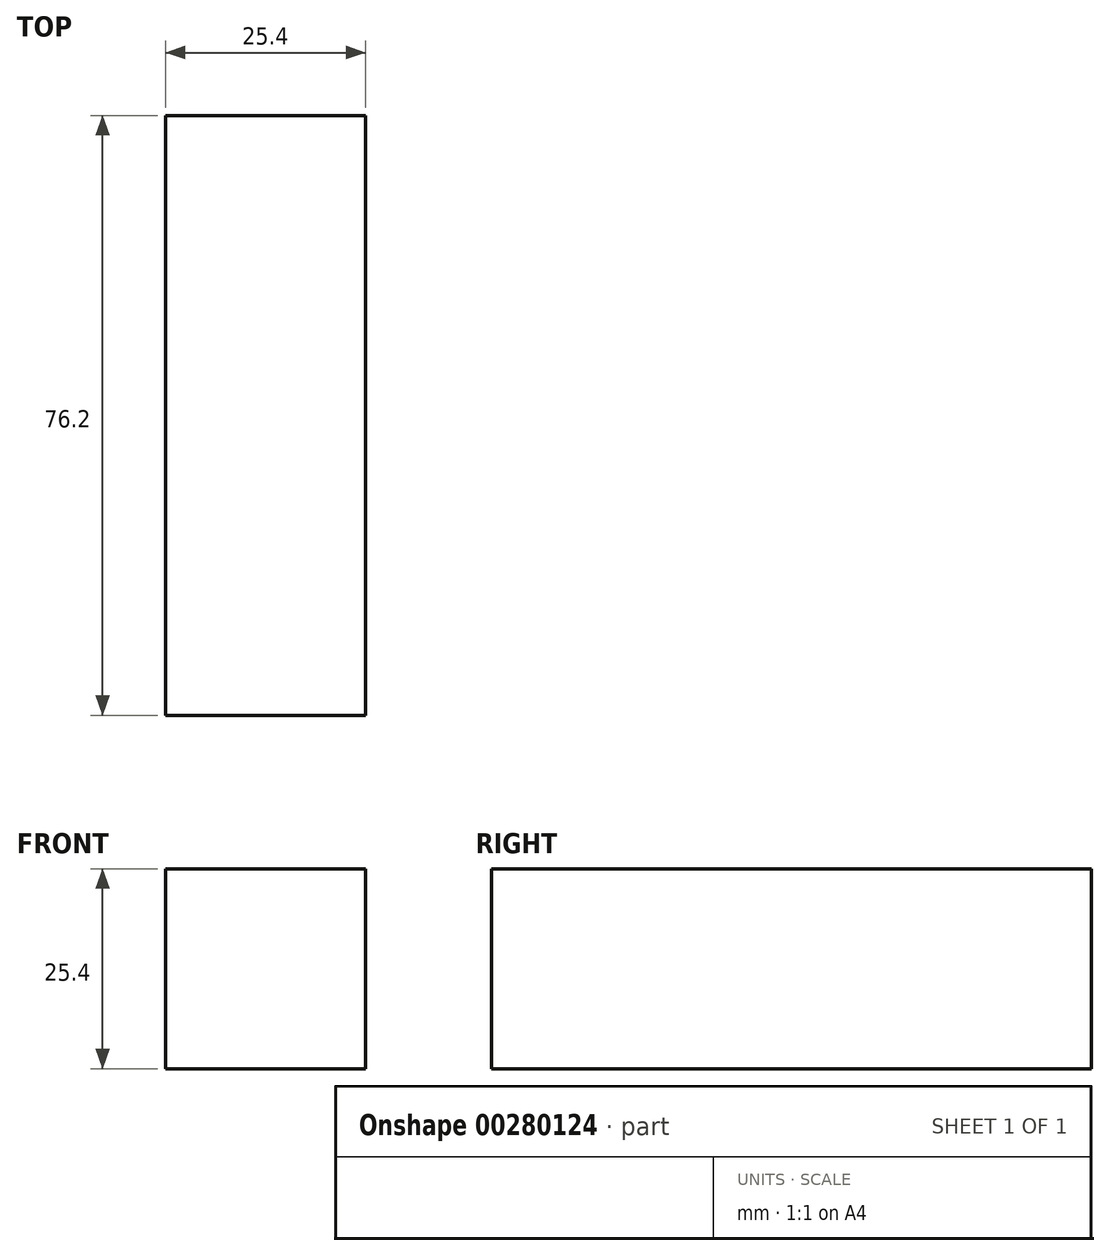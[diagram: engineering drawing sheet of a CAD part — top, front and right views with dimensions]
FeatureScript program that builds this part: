
annotation { "Feature Type Name" : "Feature", "Feature Type Description" : "" }
export const myFeature = defineFeature(function(context is Context, id is Id, definition is map)
    precondition{}
    {
        {
            var Q0;
            Q0=qCreatedBy(makeId("Front.planeOp"),FACE);
            var sketch = newSketch(context, id + "F0", { "sketchPlane" : qUnion([Q0])});
            skLineSegment(sketch, "E0.bottom", {"start": v(-42.21, 5.82) * mm, "end": v(-16.81, 5.82) * mm});
            skLineSegment(sketch, "E0.top", {"start": v(-42.21, -19.58) * mm, "end": v(-16.81, -19.58) * mm});
            skLineSegment(sketch, "E0.left", {"start": v(-42.21, 5.82) * mm, "end": v(-42.21, -19.58) * mm});
            skLineSegment(sketch, "E0.right", {"start": v(-16.81, 5.82) * mm, "end": v(-16.81, -19.58) * mm});
            skSolve(sketch);
        }
        {
            var Q0;
            Q0 = qSketchRegion(id + "F0", true);
            extrude(context, id + "F1", {"entities" : qUnion([Q0]), "depth" : 76.2 * mm});
        }
    });
